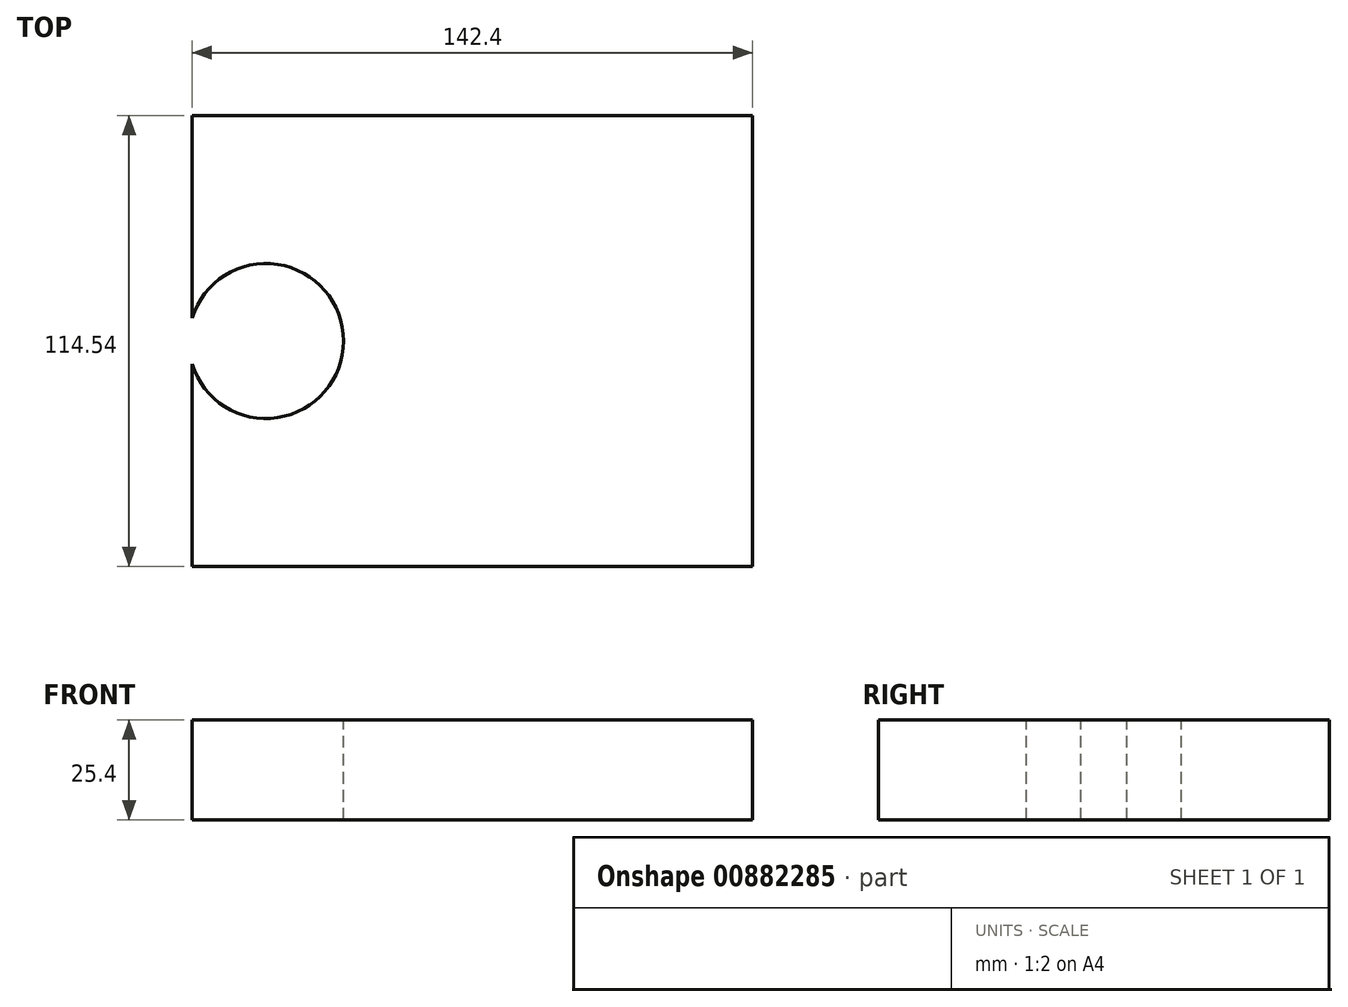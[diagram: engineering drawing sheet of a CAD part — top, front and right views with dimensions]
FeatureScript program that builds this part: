
annotation { "Feature Type Name" : "Feature", "Feature Type Description" : "" }
export const myFeature = defineFeature(function(context is Context, id is Id, definition is map)
    precondition{}
    {
        {
            var Q0;
            Q0=qCreatedBy(makeId("Top.planeOp"),FACE);
            var sketch = newSketch(context, id + "F0", { "sketchPlane" : qUnion([Q0])});
            skLineSegment(sketch, "E0.bottom", {"start": v(-71.2, 57.27) * mm, "end": v(71.2, 57.27) * mm});
            skLineSegment(sketch, "E0.top", {"start": v(-71.2, -57.27) * mm, "end": v(71.2, -57.27) * mm});
            skLineSegment(sketch, "E0.left", {"start": v(-71.2, 57.27) * mm, "end": v(-71.2, -57.27) * mm});
            skLineSegment(sketch, "E0.right", {"start": v(71.2, 57.27) * mm, "end": v(71.2, -57.27) * mm});
            skPoint(sketch, "E0.middle", {"position": v(0, 0) * mm});
            skSolve(sketch);
        }
        {
            var Q0;
            Q0 = qSketchRegion(id + "F0", true);
            extrude(context, id + "F1", {"entities" : qUnion([Q0]), "depth" : 25.4 * mm, "offsetDistance" : 25.4 * mm});
        }
        {
            var Q0;
            Q0=makeQuery(id+"F1.opExtrude","CAP_FACE",FACE,{"disambiguationData":[OSD([sQuery(id+"F0.wireOp",EDGE,"E0.bottom"),sQuery(id+"F0.wireOp",EDGE,"E0.top"),sQuery(id+"F0.wireOp",EDGE,"E0.left"),sQuery(id+"F0.wireOp",EDGE,"E0.right")])],"isStart":false});
            var sketch = newSketch(context, id + "F2", { "sketchPlane" : qUnion([Q0])});
            skCircle(sketch, "E1", {"center": v(-52.4, 0) * mm, "radius": 19.83 * mm});
            skSolve(sketch);
        }
        {
            var Q0;
            Q0=sQuery(id+"F2.wireOp",VERTEX,"E1.center");
            var Q1;
            Q1=makeQuery(id+"F1.opExtrude","SWEPT_BODY",BODY,{"disambiguationData":[OSD([sQuery(id+"F0.wireOp",EDGE,"E0.bottom"),sQuery(id+"F0.wireOp",EDGE,"E0.top"),sQuery(id+"F0.wireOp",EDGE,"E0.left"),sQuery(id+"F0.wireOp",EDGE,"E0.right")])]});
            hole(context, id + "F3", {"style" : HoleStyle.SIMPLE, "endStyle" : HoleEndStyle.THROUGH, "holeDiameter" : 39.37 * mm, "majorDiameter" : 6.35 * mm, "isTappedThrough" : true, "tappedDepth" : 12.7 * mm, "tapClearance" : 3, "locations" : qUnion([Q0]), "scope" : qUnion([Q1])});
        }
    });
